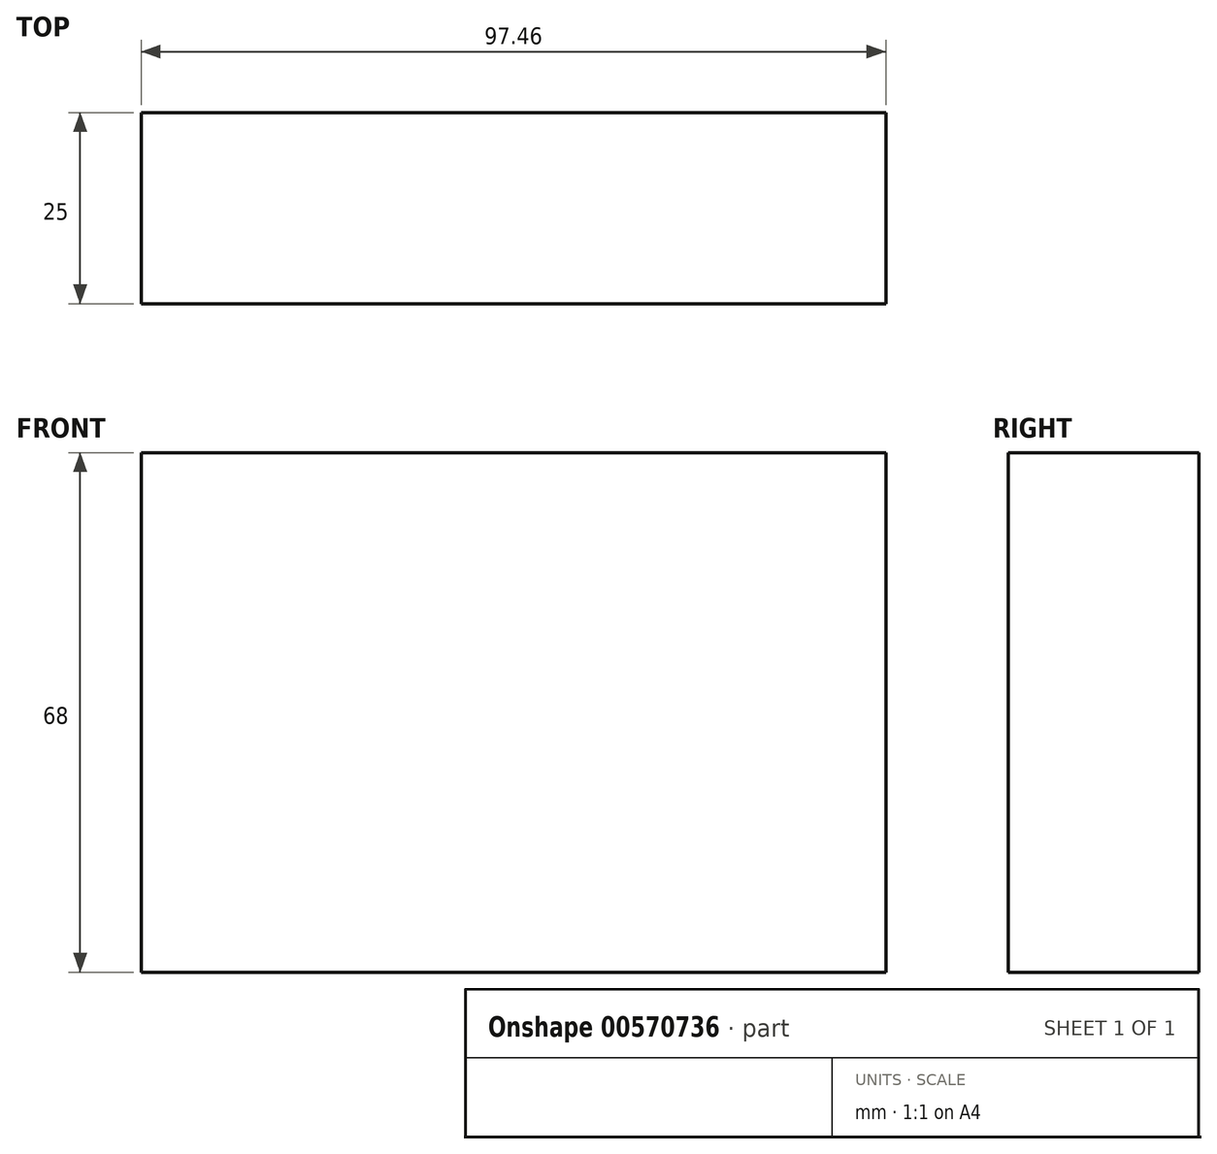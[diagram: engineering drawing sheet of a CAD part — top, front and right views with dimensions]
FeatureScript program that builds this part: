
annotation { "Feature Type Name" : "Feature", "Feature Type Description" : "" }
export const myFeature = defineFeature(function(context is Context, id is Id, definition is map)
    precondition{}
    {
        {
            var Q0;
            Q0=qCreatedBy(makeId("Front.planeOp"),FACE);
            var sketch = newSketch(context, id + "F0", { "sketchPlane" : qUnion([Q0])});
            skLineSegment(sketch, "E0.bottom", {"start": v(-66.76, -10.93) * mm, "end": v(-164.22, -10.93) * mm});
            skLineSegment(sketch, "E0.top", {"start": v(-66.76, 57.07) * mm, "end": v(-164.22, 57.07) * mm});
            skLineSegment(sketch, "E0.left", {"start": v(-66.76, -10.93) * mm, "end": v(-66.76, 57.07) * mm});
            skLineSegment(sketch, "E0.right", {"start": v(-164.22, -10.93) * mm, "end": v(-164.22, 57.07) * mm});
            skPoint(sketch, "E0.middle", {"position": v(-115.5, 23.07) * mm});
            skSolve(sketch);
        }
        {
            var Q0;
            Q0=qSketchRegion(id+"F0",true);
            extrude(context, id + "F1", {"entities" : qUnion([Q0]), "depth" : 25 * mm, "offsetDistance" : 25 * mm});
        }
    });
